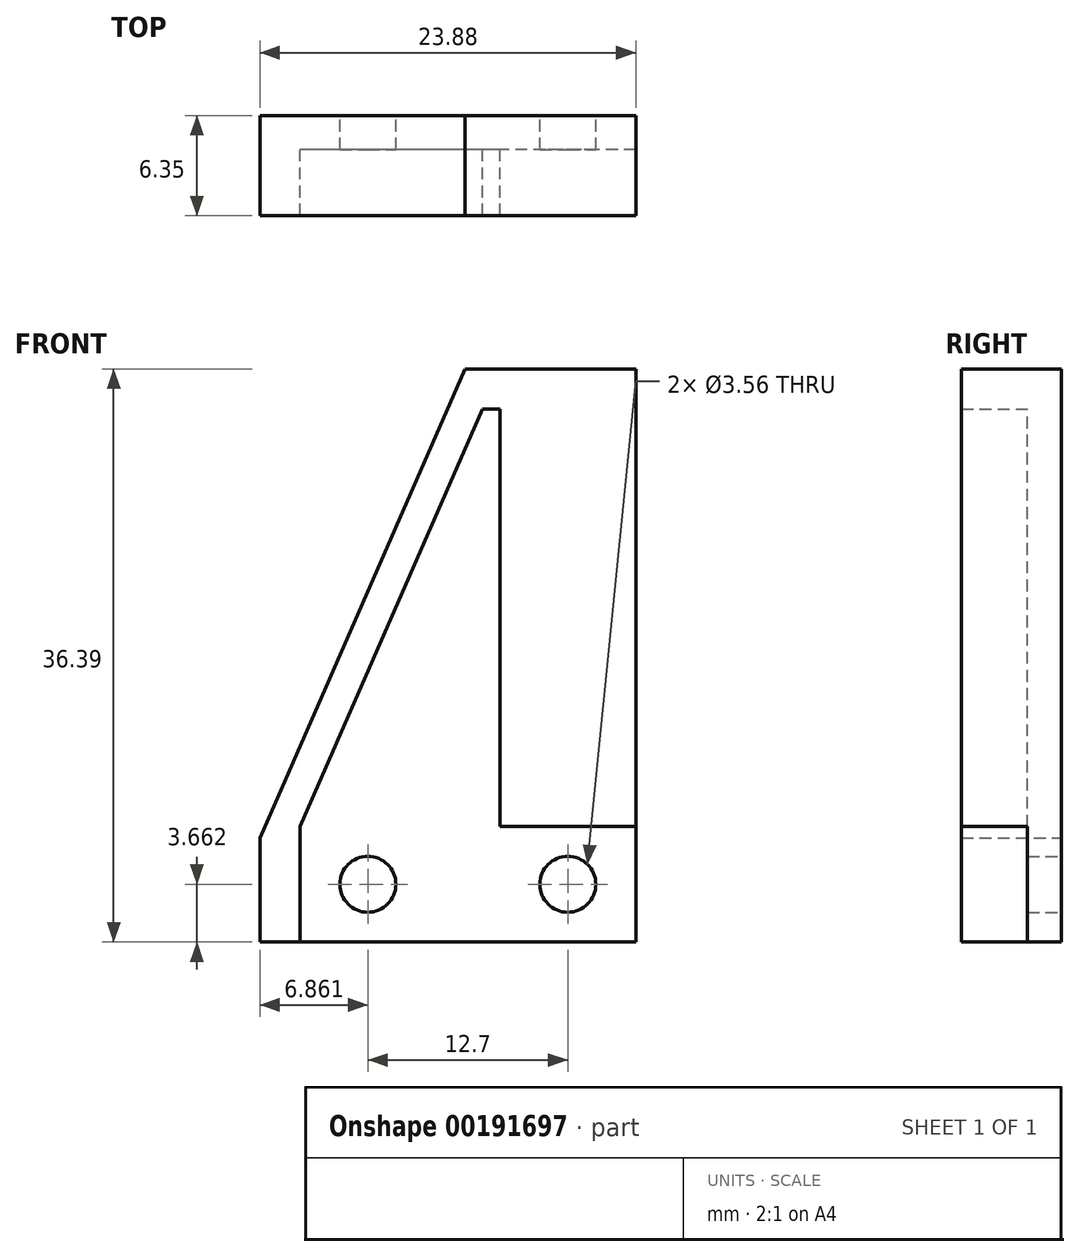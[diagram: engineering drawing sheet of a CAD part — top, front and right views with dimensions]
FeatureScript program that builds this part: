
annotation { "Feature Type Name" : "Feature", "Feature Type Description" : "" }
export const myFeature = defineFeature(function(context is Context, id is Id, definition is map)
    precondition{}
    {
        {
            var Q0;
            Q0=qCreatedBy(makeId("Front.planeOp"),FACE);
            var sketch = newSketch(context, id + "F0", { "sketchPlane" : qUnion([Q0])});
            skLineSegment(sketch, "E0.bottom", {"start": v(-13.9, -13.8) * mm, "end": v(7.43, -13.8) * mm});
            skLineSegment(sketch, "E0.top", {"start": v(-1.2, 22.6) * mm, "end": v(7.43, 22.6) * mm});
            skLineSegment(sketch, "E0.right", {"start": v(7.43, -13.8) * mm, "end": v(7.43, 22.6) * mm});
            skLineSegment(sketch, "E1", {"start": v(-13.9, -13.8) * mm, "end": v(-13.9, -6.46) * mm});
            skCircle(sketch, "E2", {"center": v(-9.59, -10.13) * mm, "radius": 1.78 * mm});
            skPoint(sketch, "E2.centerSnap0", {"position": v(-13.9, -10.13) * mm});
            skCircle(sketch, "E3", {"center": v(3.11, -10.13) * mm, "radius": 1.78 * mm});
            skCircle(sketch, "E4", {"center": v(3.11, 16.25) * mm, "radius": 1.78 * mm, "construction": true});
            skPoint(sketch, "E4.centerSnap0", {"position": v(3.11, 22.6) * mm});
            skCircle(sketch, "E5", {"center": v(3.11, 3.55) * mm, "radius": 1.78 * mm, "construction": true});
            skLineSegment(sketch, "E6", {"start": v(-13.9, -6.46) * mm, "end": v(-2.32, 20.06) * mm});
            skLineSegment(sketch, "E7", {"start": v(-3.43, 22.6) * mm, "end": v(-13.9, -1.38) * mm});
            skLineSegment(sketch, "E8", {"start": v(-3.43, 22.6) * mm, "end": v(-1.2, 22.6) * mm});
            skLineSegment(sketch, "E9", {"start": v(-13.9, -13.8) * mm, "end": v(-16.45, -13.8) * mm});
            skLineSegment(sketch, "E10", {"start": v(-13.9, -1.38) * mm, "end": v(-16.45, -7.2) * mm});
            skLineSegment(sketch, "E11", {"start": v(-16.45, -13.8) * mm, "end": v(-16.45, -7.2) * mm});
            skLineSegment(sketch, "E12", {"start": v(-13.9, -6.46) * mm, "end": v(7.43, -6.46) * mm});
            skLineSegment(sketch, "E13", {"start": v(-13.9, -6.46) * mm, "end": v(-16.13, -6.46) * mm});
            skLineSegment(sketch, "E14.bottom", {"start": v(7.43, 22.6) * mm, "end": v(-1.2, 22.6) * mm});
            skLineSegment(sketch, "E14.top", {"start": v(7.43, -6.46) * mm, "end": v(-1.2, -6.46) * mm});
            skLineSegment(sketch, "E14.left", {"start": v(7.43, 22.6) * mm, "end": v(7.43, -6.46) * mm});
            skLineSegment(sketch, "E14.right", {"start": v(-1.2, 20.06) * mm, "end": v(-1.2, -6.46) * mm});
            skLineSegment(sketch, "E15", {"start": v(-2.32, 20.06) * mm, "end": v(-1.2, 20.06) * mm});
            skSolve(sketch);
        }
        {
            var Q0;
            Q0=qSketchRegion(id+"F0",true);
            var Q1;
            Q1=makeQuery(id+"F0.imprint","IMPRINT",FACE,{"disambiguationData":[TD([[makeQuery(id+"F0.imprint","IMPRINT",EDGE,{"derivedFrom":sQuery(id+"F0.wireOp",EDGE,"E6")}),-1.0]])]});
            extrude(context, id + "F1", {"entities" : qUnion([Q0, Q1]), "depth" : 2.16 * mm});
        }
        {
            var Q0;
            Q0=makeQuery(id+"F0.imprint","IMPRINT",FACE,{"disambiguationData":[TD([[makeQuery(id+"F0.imprint","IMPRINT",EDGE,{"derivedFrom":sQuery(id+"F0.wireOp",EDGE,"E6")}),1.0]])]});
            var Q1;
            Q1=makeQuery(id+"F0.imprint","IMPRINT",FACE,{"disambiguationData":[TD([[makeQuery(id+"F0.imprint","IMPRINT",EDGE,{"derivedFrom":sQuery(id+"F0.wireOp",EDGE,"E1")}),1.0]])]});
            var Q2;
            Q2=makeQuery(id+"F0.imprint","IMPRINT",FACE,{"disambiguationData":[TD([[makeQuery(id+"F0.imprint","IMPRINT",EDGE,{"derivedFrom":sQuery(id+"F0.wireOp",EDGE,"E4")}),-1.0]])]});
            extrude(context, id + "F2", {"entities" : qUnion([Q0, Q1, Q2]), "operationType" : NewBodyOperationType.ADD, "depth" : 6.35 * mm});
        }
    });
